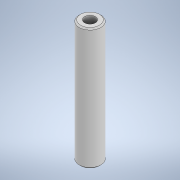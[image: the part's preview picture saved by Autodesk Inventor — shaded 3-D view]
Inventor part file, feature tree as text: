
AUTODESK INVENTOR PART (.ipt)
format: ipt  version: 2020 (Build 240168000, 168)  size: 106,496 bytes
history: native  units: mm
features: extrude x2, sketch x2, chamfer x1
ambient origin geometry x8: Origin, YZ Plane, XZ Plane, XY Plane, X Axis, Y Axis, Z Axis, Center Point
bodies: Solid1 (feature_tree)
feature tree (5):
  extrude  "Extrusion1"  Depth=45.0mm TaperAngle=0.0deg
  chamfer  "Chamfer1"  Distance=2.0mm Angle=45.0deg
  extrude  "Extrusion2"  Depth=45.0mm TaperAngle=0.0deg
  sketch  "Sketch1"  dims[d0=8.0mm d1=45.0mm d2=0.0mm d3=0.5mm d4=2.0mm d5=45.0deg]
  sketch  "Sketch2"  dims[d6=4.0mm d7=45.0mm d8=0.0mm]
